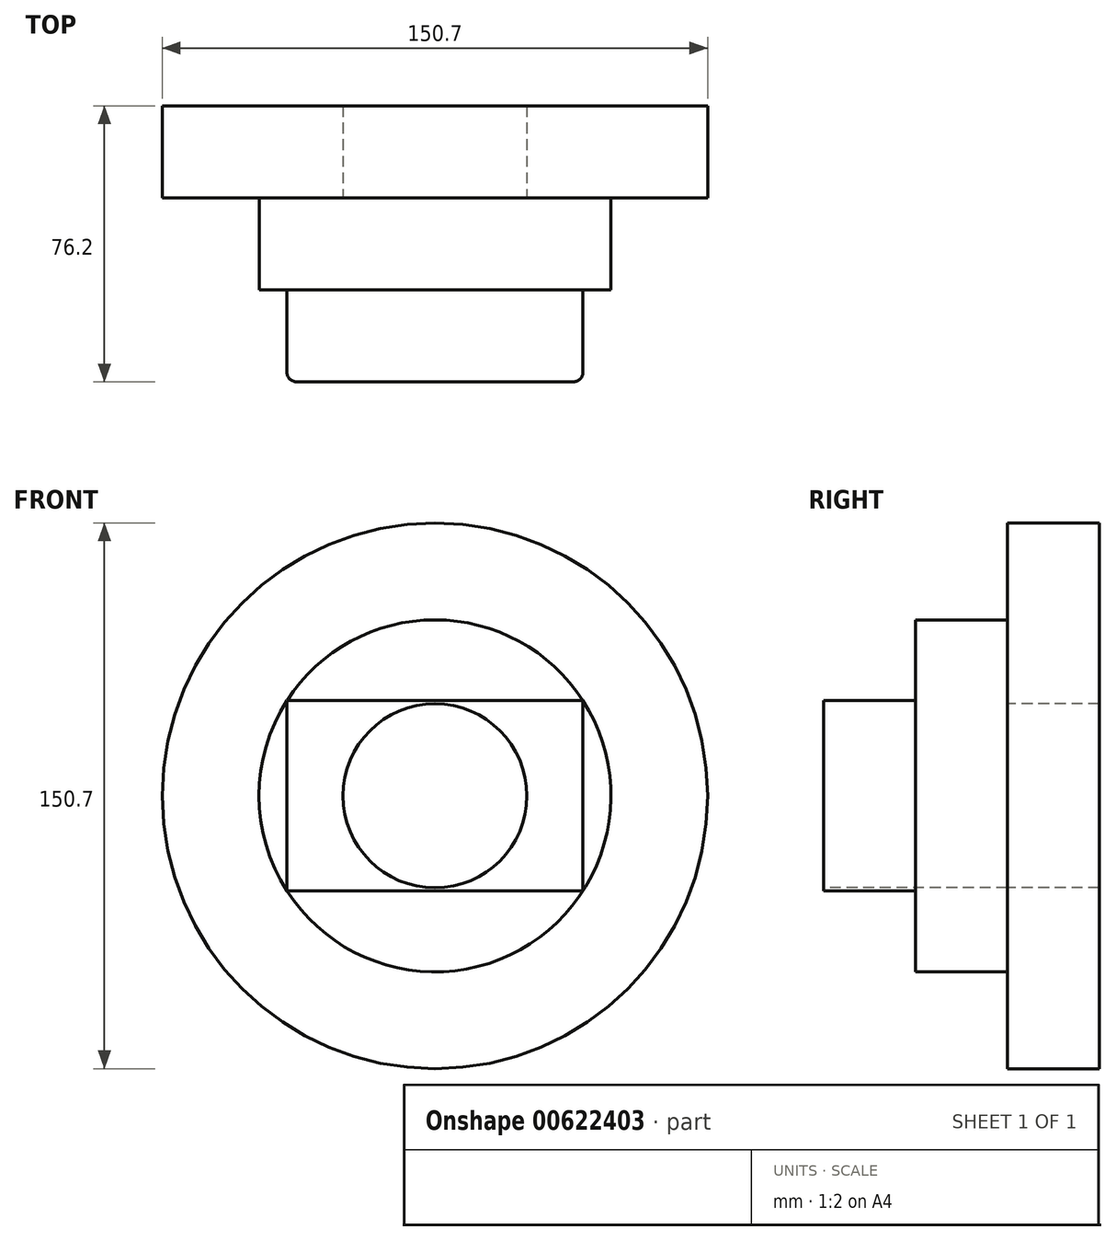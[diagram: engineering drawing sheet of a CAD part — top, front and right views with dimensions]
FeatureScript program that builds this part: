
annotation { "Feature Type Name" : "Feature", "Feature Type Description" : "" }
export const myFeature = defineFeature(function(context is Context, id is Id, definition is map)
    precondition{}
    {
        {
            var Q0;
            Q0=qCreatedBy(makeId("Front.planeOp"),FACE);
            var sketch = newSketch(context, id + "F0", { "sketchPlane" : qUnion([Q0])});
            skCircle(sketch, "E0", {"center": v(0, 0) * mm, "radius": 6.54 * mm});
            skCircle(sketch, "E1", {"center": v(0, 0) * mm, "radius": 12.15 * mm});
            skCircle(sketch, "E2", {"center": v(0, 0) * mm, "radius": 75.35 * mm});
            skSolve(sketch);
        }
        {
            var Q0;
            Q0 = qSketchRegion(id + "F0", true);
            var sketch = newSketch(context, id + "F1", { "sketchPlane" : qUnion([Q0])});
            skSolve(sketch);
        }
        {
            var Q0;
            Q0 = qSketchRegion(id + "F0", true);
            var Q1;
            Q1=makeQuery(id+"F1.imprint","IMPRINT",FACE,{"disambiguationData":[TD([[makeQuery(id+"F1.imprint","IMPRINT",EDGE,{"derivedFrom":makeQuery(id+"F0.imprint","IMPRINT",EDGE,{"derivedFrom":sQuery(id+"F0.wireOp",EDGE,"E1")})}),-1.0]])]});
            extrude(context, id + "F2", {"entities" : qUnion([Q0, Q1]), "depth" : 25.4 * mm, "offsetDistance" : 25.4 * mm});
        }
        {
            var Q0;
            {var subQ0=sQuery(id+"F0.wireOp",EDGE,"E2");var subQ1=sQuery(id+"F0.wireOp",EDGE,"E1");Q0=makeQuery(id+"F2.opExtrude","CAP_FACE",FACE,{"disambiguationData":[OSD([subQ1,subQ0]),TDD([makeQuery(id+"F1.imprint","IMPRINT",EDGE,{"derivedFrom":makeQuery(id+"F0.imprint","IMPRINT",EDGE,{"derivedFrom":subQ1})}),makeQuery(id+"F1.imprint","IMPRINT",EDGE,{"derivedFrom":makeQuery(id+"F0.imprint","IMPRINT",EDGE,{"derivedFrom":subQ0})})])],"isStart":false});}
            var sketch = newSketch(context, id + "F3", { "sketchPlane" : qUnion([Q0])});
            skCircle(sketch, "E3", {"center": v(0, 0) * mm, "radius": 48.61 * mm});
            skSolve(sketch);
        }
        {
            var Q0;
            Q0 = qSketchRegion(id + "F3", true);
            extrude(context, id + "F4", {"entities" : qUnion([Q0]), "depth" : 25.4 * mm, "offsetDistance" : 25.4 * mm});
        }
        {
            var Q0;
            Q0=makeQuery(id+"F4.opExtrude","CAP_FACE",FACE,{"disambiguationData":[OSD([sQuery(id+"F3.wireOp",EDGE,"E3")])],"isStart":false});
            var sketch = newSketch(context, id + "F5", { "sketchPlane" : qUnion([Q0])});
            skLineSegment(sketch, "E4.bottom", {"start": v(40.86, 26.33) * mm, "end": v(-40.88, 26.33) * mm});
            skLineSegment(sketch, "E4.top", {"start": v(40.86, -26.3) * mm, "end": v(-40.88, -26.3) * mm});
            skLineSegment(sketch, "E4.left", {"start": v(40.86, 26.33) * mm, "end": v(40.86, -26.3) * mm});
            skLineSegment(sketch, "E4.right", {"start": v(-40.88, 26.33) * mm, "end": v(-40.88, -26.3) * mm});
            skSolve(sketch);
        }
        {
            var Q0;
            Q0 = qSketchRegion(id + "F5", true);
            extrude(context, id + "F6", {"entities" : qUnion([Q0]), "operationType" : NewBodyOperationType.ADD, "depth" : 25.4 * mm, "offsetDistance" : 25.4 * mm});
        }
        {
            var Q0;
            Q0=makeQuery(id+"F6.opExtrude","CAP_FACE",FACE,{"disambiguationData":[OSD([sQuery(id+"F5.wireOp",EDGE,"E4.bottom"),sQuery(id+"F5.wireOp",EDGE,"E4.top"),sQuery(id+"F5.wireOp",EDGE,"E4.left"),sQuery(id+"F5.wireOp",EDGE,"E4.right")])],"isStart":false});
            var sketch = newSketch(context, id + "F7", { "sketchPlane" : qUnion([Q0])});
            skCircle(sketch, "E5", {"center": v(0, 0) * mm, "radius": 24.59 * mm});
            skSolve(sketch);
        }
        {
            var Q0;
            Q0=sQuery(id+"F7.wireOp",VERTEX,"E5.center");
            var Q1;
            Q1=makeQuery(id+"F4.opExtrude","SWEPT_BODY",BODY,{"disambiguationData":[OSD([sQuery(id+"F3.wireOp",EDGE,"E3")])]});
            var Q2;
            {var subQ0=sQuery(id+"F0.wireOp",EDGE,"E2");var subQ1=sQuery(id+"F0.wireOp",EDGE,"E1");Q2=makeQuery(id+"F2.opExtrude","SWEPT_BODY",BODY,{"disambiguationData":[OSD([subQ1,subQ0]),TDD([makeQuery(id+"F0.imprint","IMPRINT",EDGE,{"derivedFrom":subQ1}),makeQuery(id+"F0.imprint","IMPRINT",EDGE,{"derivedFrom":subQ0})])]});}
            var Q3;
            {var subQ0=sQuery(id+"F0.wireOp",EDGE,"E2");var subQ1=sQuery(id+"F0.wireOp",EDGE,"E1");Q3=makeQuery(id+"F2.opExtrude","SWEPT_BODY",BODY,{"disambiguationData":[OSD([subQ1,subQ0]),TDD([makeQuery(id+"F1.imprint","IMPRINT",EDGE,{"derivedFrom":makeQuery(id+"F0.imprint","IMPRINT",EDGE,{"derivedFrom":subQ1})}),makeQuery(id+"F1.imprint","IMPRINT",EDGE,{"derivedFrom":makeQuery(id+"F0.imprint","IMPRINT",EDGE,{"derivedFrom":subQ0})})])]});}
            hole(context, id + "F8", {"style" : HoleStyle.SIMPLE, "endStyle" : HoleEndStyle.THROUGH, "holeDiameter" : 50.8 * mm, "majorDiameter" : 6.35 * mm, "isTappedThrough" : true, "tappedDepth" : 12.7 * mm, "tapClearance" : 3, "locations" : qUnion([Q0]), "scope" : qUnion([Q1, Q2, Q3])});
        }
        {
            var Q0;
            Q0=makeQuery(id+"F6.opExtrude","CAP_EDGE",EDGE,{"disambiguationData":[OSD([sQuery(id+"F5.wireOp",EDGE,"E4.right")])],"isStart":false});
            var Q1;
            Q1=makeQuery(id+"F6.opExtrude","CAP_EDGE",EDGE,{"disambiguationData":[OSD([sQuery(id+"F5.wireOp",EDGE,"E4.left")])],"isStart":false});
            fillet(context, id + "F9", {"entities" : qUnion([Q0, Q1]), "radius" : 2.54 * mm, "tangentPropagation" : true, "allowEdgeOverflow" : false});
        }
    });
